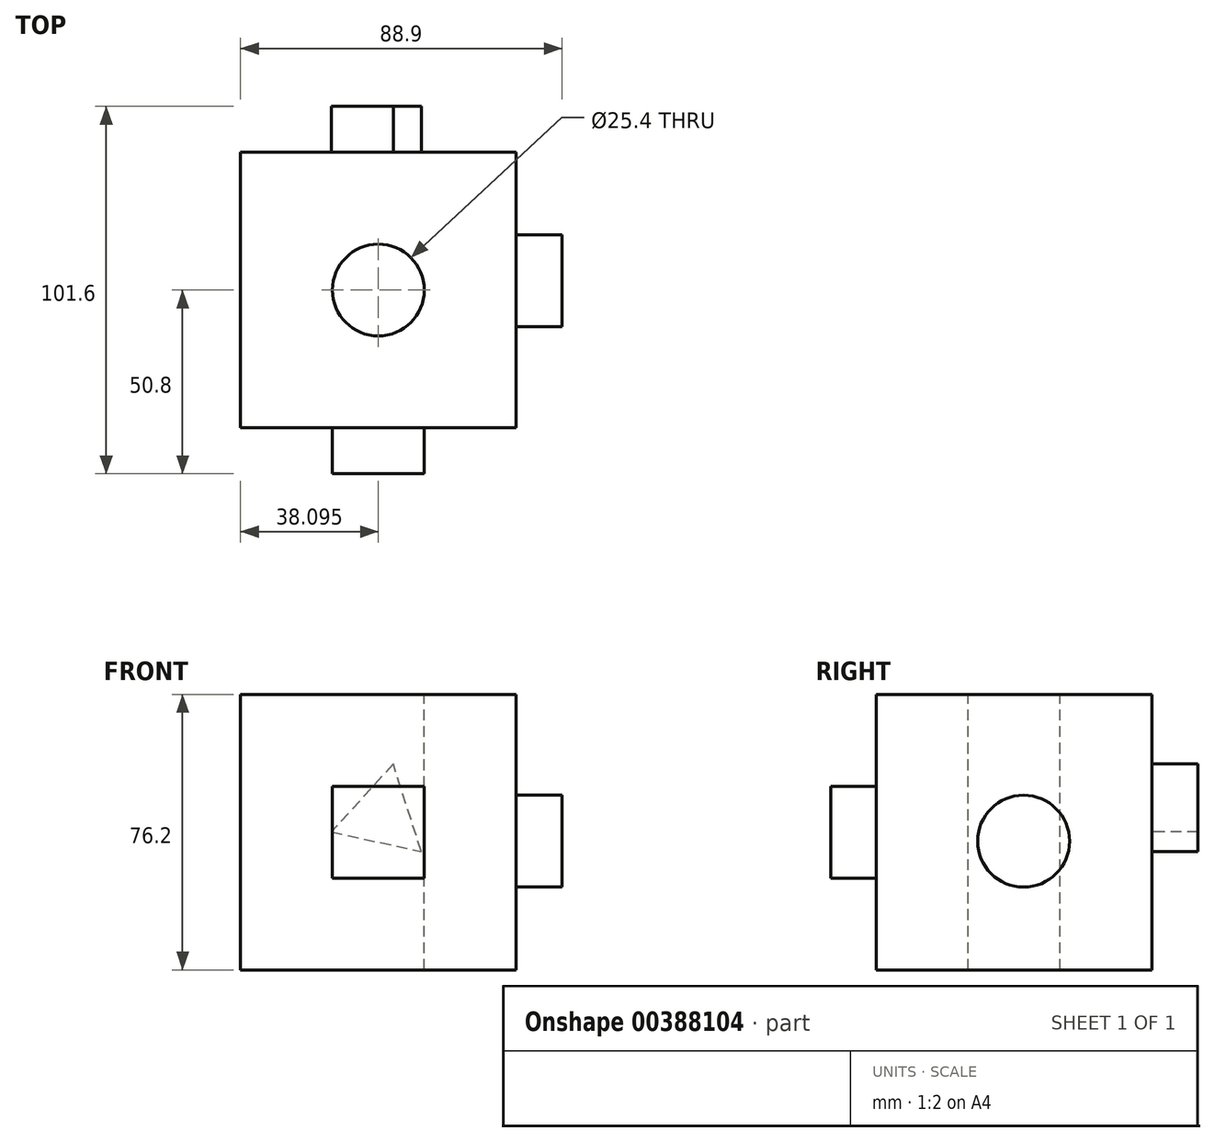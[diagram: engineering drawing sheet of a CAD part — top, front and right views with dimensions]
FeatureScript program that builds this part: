
annotation { "Feature Type Name" : "Feature", "Feature Type Description" : "" }
export const myFeature = defineFeature(function(context is Context, id is Id, definition is map)
    precondition{}
    {
        {
            var Q0;
            Q0=qCreatedBy(makeId("Front.planeOp"),FACE);
            var sketch = newSketch(context, id + "F0", { "sketchPlane" : qUnion([Q0])});
            skLineSegment(sketch, "E0.bottom", {"start": v(9.33, -4.66) * mm, "end": v(-66.87, -4.66) * mm});
            skLineSegment(sketch, "E0.top", {"start": v(9.33, 71.54) * mm, "end": v(-66.87, 71.54) * mm});
            skLineSegment(sketch, "E0.left", {"start": v(9.33, -4.66) * mm, "end": v(9.33, 71.54) * mm});
            skLineSegment(sketch, "E0.right", {"start": v(-66.87, -4.66) * mm, "end": v(-66.87, 71.54) * mm});
            skPoint(sketch, "E0.middle", {"position": v(-28.77, 33.44) * mm});
            skSolve(sketch);
        }
        {
            var Q0;
            Q0 = qSketchRegion(id + "F0", true);
            extrude(context, id + "F1", {"entities" : qUnion([Q0]), "depth" : 76.2 * mm});
        }
        {
            var Q0;
            Q0=makeQuery(id+"F1.opExtrude","SWEPT_FACE",FACE,{"disambiguationData":[OSD([sQuery(id+"F0.wireOp",EDGE,"E0.top")])]});
            var sketch = newSketch(context, id + "F2", { "sketchPlane" : qUnion([Q0])});
            skPoint(sketch, "E1", {"position": v(-28.77, -38.1) * mm});
            skSolve(sketch);
        }
        {
            var Q0;
            Q0=sQuery(id+"F2.wireOp",VERTEX,"E1");
            var Q1;
            Q1=makeQuery(id+"F1.opExtrude","SWEPT_BODY",BODY,{"disambiguationData":[OSD([sQuery(id+"F0.wireOp",EDGE,"E0.bottom"),sQuery(id+"F0.wireOp",EDGE,"E0.top"),sQuery(id+"F0.wireOp",EDGE,"E0.left"),sQuery(id+"F0.wireOp",EDGE,"E0.right")])]});
            hole(context, id + "F3", {"style" : HoleStyle.SIMPLE, "endStyle" : HoleEndStyle.THROUGH, "holeDiameter" : 25.4 * mm, "isTappedThrough" : true, "tappedDepth" : 12.7 * mm, "tapClearance" : 3, "locations" : qUnion([Q0]), "scope" : qUnion([Q1])});
        }
        {
            var Q0;
            Q0=makeQuery(id+"F1.opExtrude","CAP_FACE",FACE,{"disambiguationData":[OSD([sQuery(id+"F0.wireOp",EDGE,"E0.bottom"),sQuery(id+"F0.wireOp",EDGE,"E0.top"),sQuery(id+"F0.wireOp",EDGE,"E0.left"),sQuery(id+"F0.wireOp",EDGE,"E0.right")])],"isStart":false});
            var sketch = newSketch(context, id + "F4", { "sketchPlane" : qUnion([Q0])});
            skLineSegment(sketch, "E2.bottom", {"start": v(-41.47, 46.14) * mm, "end": v(-16.07, 46.14) * mm});
            skLineSegment(sketch, "E2.top", {"start": v(-41.47, 20.74) * mm, "end": v(-16.07, 20.74) * mm});
            skLineSegment(sketch, "E2.left", {"start": v(-41.47, 46.14) * mm, "end": v(-41.47, 20.74) * mm});
            skLineSegment(sketch, "E2.right", {"start": v(-16.07, 46.14) * mm, "end": v(-16.07, 20.74) * mm});
            skSolve(sketch);
        }
        {
            var Q0;
            Q0 = qSketchRegion(id + "F4", true);
            extrude(context, id + "F5", {"entities" : qUnion([Q0]), "operationType" : NewBodyOperationType.ADD, "depth" : 12.7 * mm});
        }
        {
            var Q0;
            Q0=makeQuery(id+"F1.opExtrude","SWEPT_FACE",FACE,{"disambiguationData":[OSD([sQuery(id+"F0.wireOp",EDGE,"E0.left")])]});
            var sketch = newSketch(context, id + "F6", { "sketchPlane" : qUnion([Q0])});
            skCircle(sketch, "E3", {"center": v(-35.55, 30.93) * mm, "radius": 12.7 * mm});
            skSolve(sketch);
        }
        {
            var Q0;
            Q0 = qSketchRegion(id + "F6", true);
            extrude(context, id + "F7", {"entities" : qUnion([Q0]), "operationType" : NewBodyOperationType.ADD, "depth" : 12.7 * mm});
        }
        {
            var Q0;
            Q0=makeQuery(id+"F1.opExtrude","CAP_FACE",FACE,{"disambiguationData":[OSD([sQuery(id+"F0.wireOp",EDGE,"E0.bottom"),sQuery(id+"F0.wireOp",EDGE,"E0.top"),sQuery(id+"F0.wireOp",EDGE,"E0.left"),sQuery(id+"F0.wireOp",EDGE,"E0.right")])],"isStart":true});
            var sketch = newSketch(context, id + "F8", { "sketchPlane" : qUnion([Q0])});
            skCircle(sketch, "E4.cCircle", {"center": v(27.77, 37.95) * mm, "radius": 7.33 * mm, "construction": true});
            skLineSegment(sketch, "E4.0", {"start": v(16.9, 28.1) * mm, "end": v(24.67, 52.29) * mm});
            skLineSegment(sketch, "E4.1", {"start": v(24.67, 52.29) * mm, "end": v(41.73, 33.46) * mm});
            skLineSegment(sketch, "E4.2", {"start": v(41.73, 33.46) * mm, "end": v(16.9, 28.1) * mm});
            skPoint(sketch, "E4.0.midPoint", {"position": v(20.79, 40.2) * mm});
            skSolve(sketch);
        }
        {
            var Q0;
            Q0=makeQuery(id+"F8.imprint","IMPRINT",FACE,{"disambiguationData":[TD([[makeQuery(id+"F8.imprint","IMPRINT",EDGE,{"derivedFrom":sQuery(id+"F8.wireOp",EDGE,"E4.0")}),-1.0]])]});
            extrude(context, id + "F9", {"entities" : qUnion([Q0]), "operationType" : NewBodyOperationType.ADD, "depth" : 12.7 * mm});
        }
    });
